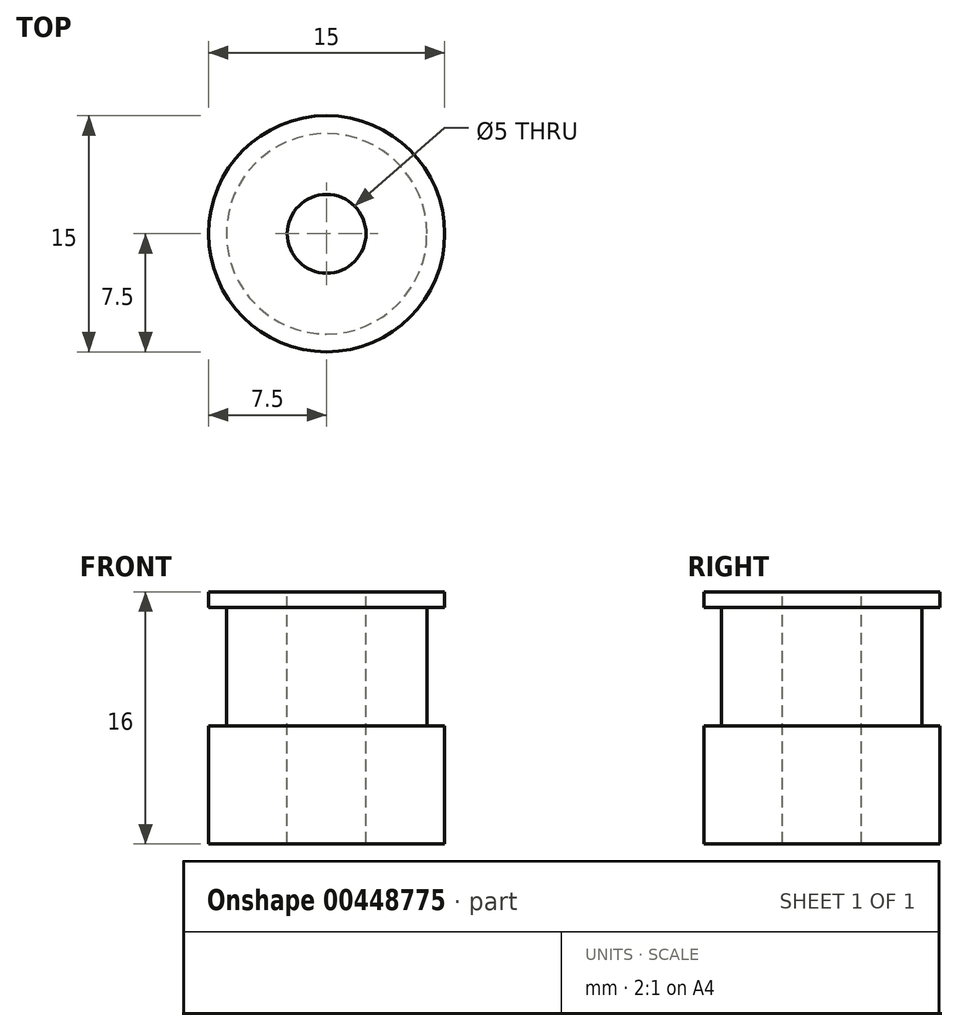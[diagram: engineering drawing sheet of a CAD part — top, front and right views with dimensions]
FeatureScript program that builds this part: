
annotation { "Feature Type Name" : "Feature", "Feature Type Description" : "" }
export const myFeature = defineFeature(function(context is Context, id is Id, definition is map)
    precondition{}
    {
        {
            var Q0;
            Q0=qCreatedBy(makeId("Front.planeOp"),FACE);
            var sketch = newSketch(context, id + "F0", { "sketchPlane" : qUnion([Q0])});
            skLineSegment(sketch, "E0", {"start": v(-7.5, 0) * mm, "end": v(-7.5, 7.5) * mm});
            skLineSegment(sketch, "E1", {"start": v(-7.5, 7.5) * mm, "end": v(-6.36, 7.5) * mm});
            skLineSegment(sketch, "E2", {"start": v(-6.37, 7.5) * mm, "end": v(-6.37, 15) * mm});
            skLineSegment(sketch, "E3", {"start": v(-6.37, 15) * mm, "end": v(-7.5, 15) * mm});
            skLineSegment(sketch, "E4", {"start": v(-7.5, 15) * mm, "end": v(-7.5, 16) * mm});
            skLineSegment(sketch, "E5", {"start": v(-7.5, 0) * mm, "end": v(-2.5, 0) * mm});
            skLineSegment(sketch, "E6", {"start": v(-7.5, 16) * mm, "end": v(-2.5, 16) * mm});
            skLineSegment(sketch, "E7", {"start": v(-2.5, 16) * mm, "end": v(-2.5, 0) * mm});
            skLineSegment(sketch, "E8", {"start": v(0, 22.6) * mm, "end": v(0, 0) * mm, "construction": true});
            skSolve(sketch);
        }
        {
            var Q0;
            Q0=makeQuery(id+"F0.imprint","IMPRINT",FACE,{"disambiguationData":[TD([[makeQuery(id+"F0.imprint","IMPRINT",EDGE,{"derivedFrom":sQuery(id+"F0.wireOp",EDGE,"E0")}),-1.0]])]});
            var Q1;
            Q1=sQuery(id+"F0.wireOp",EDGE,"E8");
            revolve(context, id + "F1", {"entities" : qUnion([Q0]), "axis" : qUnion([Q1]), "revolveType" : RevolveType.FULL});
        }
    });
